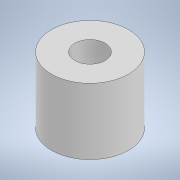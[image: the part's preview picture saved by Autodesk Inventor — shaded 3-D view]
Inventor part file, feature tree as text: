
AUTODESK INVENTOR PART (.ipt)
format: ipt  version: 2022 (Build 260153000, 153)  size: 117,248 bytes
history: native  units: in
note: dims shown in document units (in); Inventor stores cm internally (conversion verified against a paired STEP export)
features: extrude x3, sketch x3
ambient origin geometry x8: Origin, YZ Plane, XZ Plane, XY Plane, X Axis, Y Axis, Z Axis, Center Point
bodies: Solid1 (feature_tree)
feature tree (6):
  extrude  "Extrusion1"  Depth=0.2756in
  extrude  "Extrusion2"  Depth=0.1181in TaperAngle=0.0deg
  extrude  "Extrusion3"  Depth=0.1181in
  sketch  "Sketch1"  dims[d0=0.1555in d1=0.2756in]
  sketch  "Sketch2"  dims[d2=0.0354in d3=0.1181in d4=0.0in]
  sketch  "Sketch3"  dims[d5=0.1181in d6=0.0in d7=0.1083in d8=0.1181in d9=0.0in d10=0.18in]
